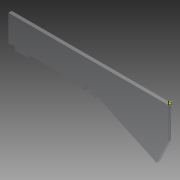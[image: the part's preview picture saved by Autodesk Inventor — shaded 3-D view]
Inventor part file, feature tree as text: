
AUTODESK INVENTOR PART (.ipt)
format: ipt  version: 2013 (Build 170138000, 138)  size: 112,640 bytes
history: native  units: in
note: dims shown in document units (in); Inventor stores cm internally (conversion verified against a paired STEP export)
features: reference x5, extrude x2, sketch x2
ambient origin geometry x8: Origin, YZ Plane, XZ Plane, XY Plane, X Axis, Y Axis, Z Axis, Center Point
bodies: Solid1 (feature_tree)
feature tree (9):
  extrude  "Extrusion1"  Depth=3.125in
  extrude  "Extrusion2"  Depth=0.125in
  sketch  "Sketch1"  dims[d0=1.0in d1=3.125in]
  sketch  "Sketch2"  dims[d2=0.25in d4=0.125in d5=0.5in d6=0.25in d7=0.125in d8=0.5in d9=1.0in d10=1.0in d11=0.125in d12=0.0in d13=1.0in d14=0.125in d15=0.0in]
  reference  "Reference1"
  reference  "Reference2"
  reference  "Reference3"
  reference  "Reference4"
  reference  "Reference5"
